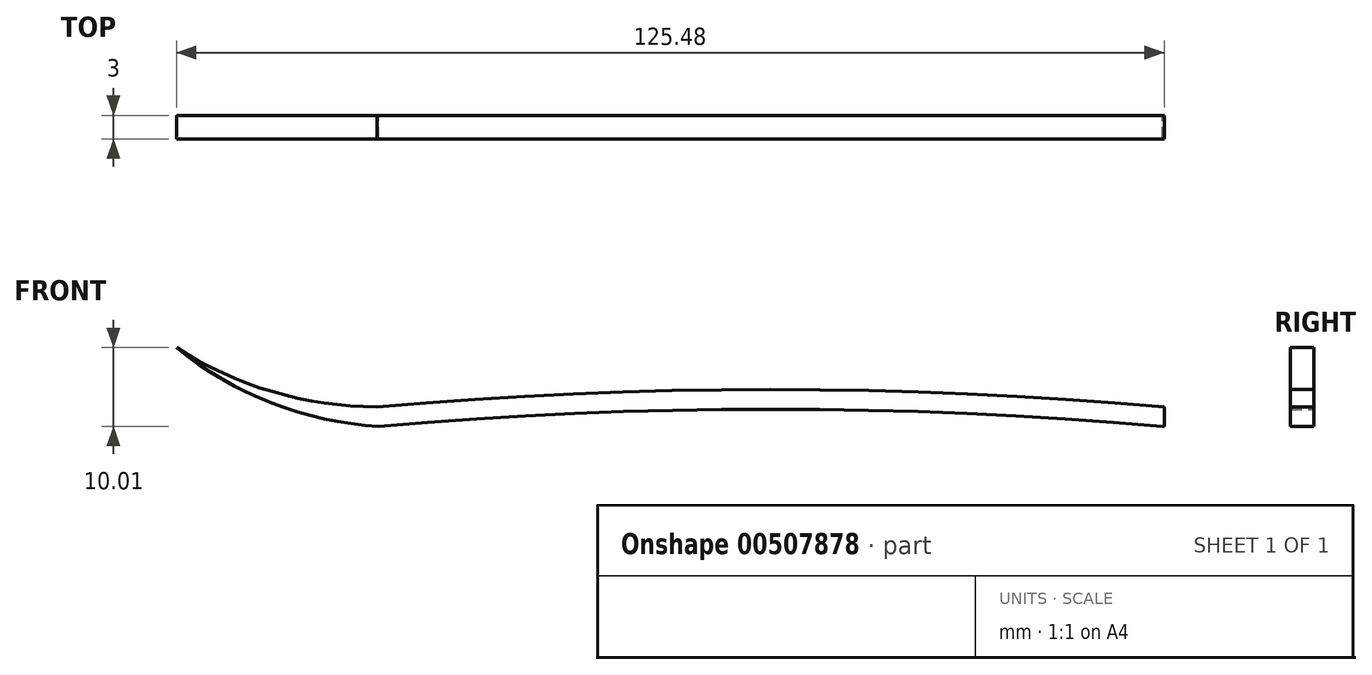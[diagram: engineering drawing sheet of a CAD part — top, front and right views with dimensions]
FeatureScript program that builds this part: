
annotation { "Feature Type Name" : "Feature", "Feature Type Description" : "" }
export const myFeature = defineFeature(function(context is Context, id is Id, definition is map)
    precondition{}
    {
        {
            var Q0;
            Q0=qCreatedBy(makeId("Front.planeOp"),FACE);
            var sketch = newSketch(context, id + "F0", { "sketchPlane" : qUnion([Q0])});
            skLineSegment(sketch, "E0", {"start": v(0, 0) * mm, "end": v(100, 0) * mm, "construction": true});
            skArc(sketch, "E1", {"start": v(100, 0) * mm, "mid": v(50, 2.19) * mm, "end": v(0, 0) * mm});
            skLineSegment(sketch, "E2", {"start": v(100, 0) * mm, "end": v(100, -2.5) * mm});
            skArc(sketch, "E3.0", {"start": v(99.78, -2.5) * mm, "mid": v(50, -0.31) * mm, "end": v(0.22, -2.5) * mm});
            skArc(sketch, "E4", {"start": v(-25.48, 7.5) * mm, "mid": v(-13.28, 1.92) * mm, "end": v(0, 0) * mm});
            skArc(sketch, "E5", {"start": v(-25.48, 7.5) * mm, "mid": v(-13.41, 0.5) * mm, "end": v(0.22, -2.5) * mm});
            skLineSegment(sketch, "E6", {"start": v(-25.48, 7.5) * mm, "end": v(-25.48, -2.5) * mm, "construction": true});
            skLineSegment(sketch, "E7", {"start": v(0, -2.5) * mm, "end": v(-25.48, -2.5) * mm, "construction": true});
            skLineSegment(sketch, "E8", {"start": v(100, -2.5) * mm, "end": v(99.78, -2.5) * mm});
            skLineSegment(sketch, "E9", {"start": v(2.9, 42.43) * mm, "end": v(0, 0) * mm, "construction": true});
            skSolve(sketch);
        }
        {
            var Q0;
            Q0=makeQuery(id+"F0.imprint","IMPRINT",FACE,{"disambiguationData":[TD([[makeQuery(id+"F0.imprint","IMPRINT",EDGE,{"derivedFrom":sQuery(id+"F0.wireOp",EDGE,"E1")}),1.0]])]});
            extrude(context, id + "F1", {"entities" : qUnion([Q0]), "depth" : 3 * mm, "offsetDistance" : 25 * mm, "symmetric" : true});
        }
    });
